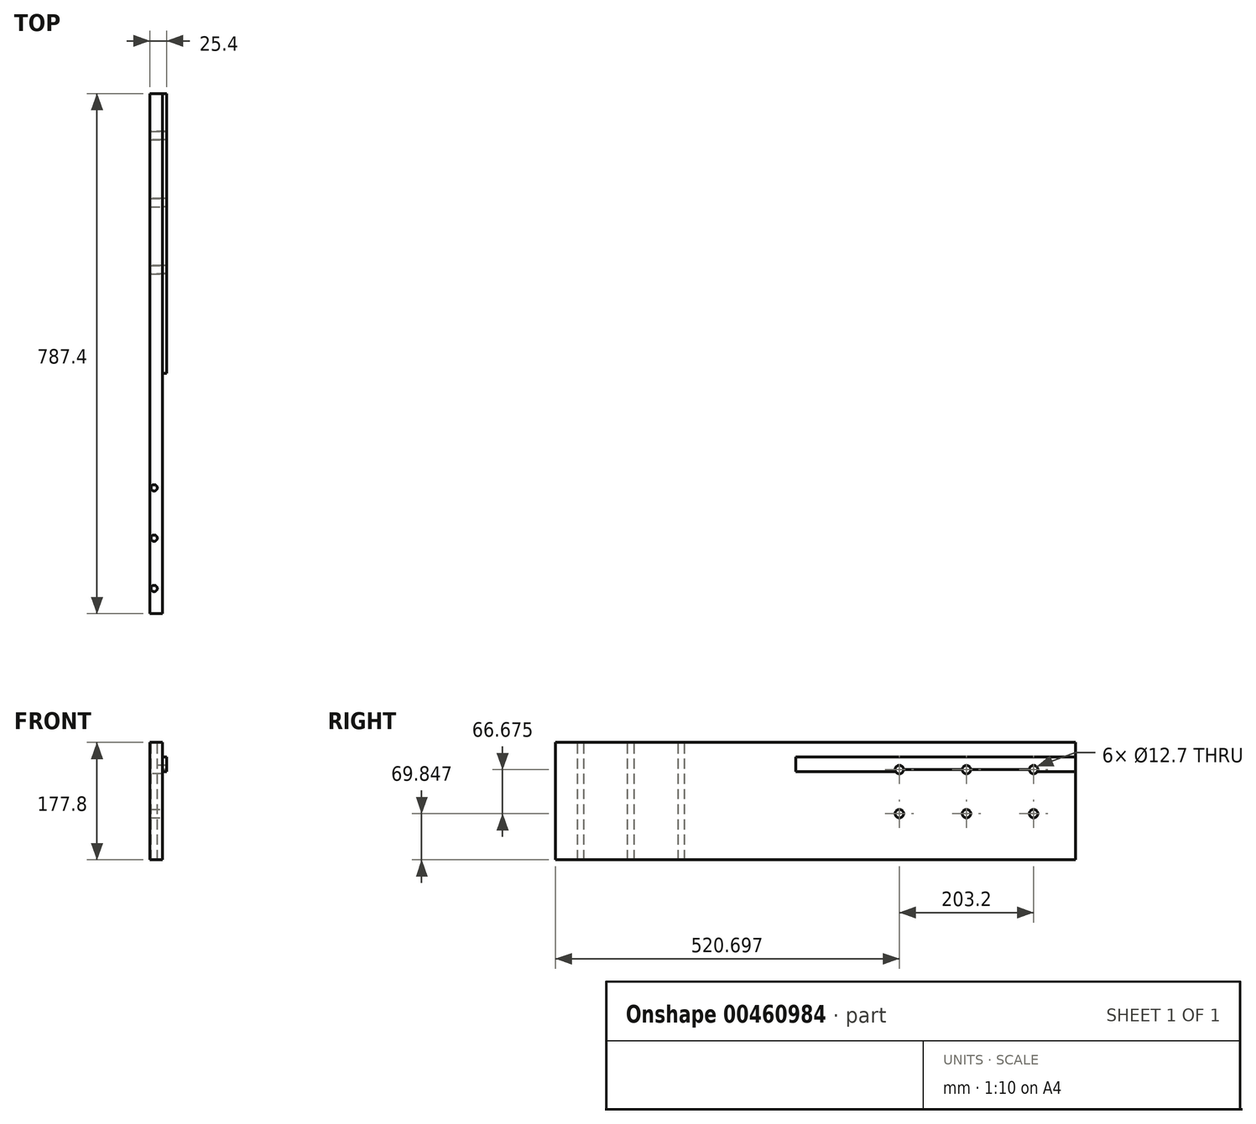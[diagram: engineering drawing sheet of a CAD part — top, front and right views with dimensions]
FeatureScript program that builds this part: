
annotation { "Feature Type Name" : "Feature", "Feature Type Description" : "" }
export const myFeature = defineFeature(function(context is Context, id is Id, definition is map)
    precondition{}
    {
        {
            var Q0;
            Q0=qCreatedBy(makeId("Right.planeOp"),FACE);
            var sketch = newSketch(context, id + "F0", { "sketchPlane" : qUnion([Q0])});
            skLineSegment(sketch, "E0.bottom", {"start": v(-363.93, 155.74) * mm, "end": v(423.47, 155.74) * mm});
            skLineSegment(sketch, "E0.top", {"start": v(-363.93, -22.06) * mm, "end": v(423.47, -22.06) * mm});
            skLineSegment(sketch, "E0.left", {"start": v(-363.93, 155.74) * mm, "end": v(-363.93, -22.06) * mm});
            skLineSegment(sketch, "E0.right", {"start": v(423.47, 155.74) * mm, "end": v(423.47, -22.06) * mm});
            skSolve(sketch);
        }
        {
            var Q0;
            Q0=makeQuery(id+"F0.imprint","IMPRINT",FACE,{"disambiguationData":[TD([[makeQuery(id+"F0.imprint","IMPRINT",EDGE,{"derivedFrom":sQuery(id+"F0.wireOp",EDGE,"E0.bottom")}),-1.0]])]});
            extrude(context, id + "F1", {"entities" : qUnion([Q0]), "depth" : 19.05 * mm});
        }
        {
            var Q0;
            Q0=makeQuery(id+"F1.opExtrude","CAP_FACE",FACE,{"disambiguationData":[OSD([sQuery(id+"F0.wireOp",EDGE,"E0.bottom"),sQuery(id+"F0.wireOp",EDGE,"E0.top"),sQuery(id+"F0.wireOp",EDGE,"E0.left"),sQuery(id+"F0.wireOp",EDGE,"E0.right")])],"isStart":false});
            var sketch = newSketch(context, id + "F2", { "sketchPlane" : qUnion([Q0])});
            skPoint(sketch, "E1", {"position": v(359.97, 47.79) * mm});
            skPoint(sketch, "E2", {"position": v(258.37, 47.79) * mm});
            skPoint(sketch, "E3", {"position": v(156.77, 47.79) * mm});
            skSolve(sketch);
        }
        {
            var Q0;
            Q0=makeQuery(id+"F1.opExtrude","SWEPT_FACE",FACE,{"disambiguationData":[OSD([sQuery(id+"F0.wireOp",EDGE,"E0.bottom")])]});
            var sketch = newSketch(context, id + "F3", { "sketchPlane" : qUnion([Q0])});
            skPoint(sketch, "E4", {"position": v(6.35, -325.83) * mm});
            skPoint(sketch, "E5", {"position": v(6.35, -249.63) * mm});
            skPoint(sketch, "E6", {"position": v(6.35, -173.43) * mm});
            skSolve(sketch);
        }
        {
            var Q0;
            Q0=sQuery(id+"F2.wireOp",VERTEX,"E3");
            var Q1;
            Q1=sQuery(id+"F2.wireOp",VERTEX,"E2");
            var Q2;
            Q2=sQuery(id+"F2.wireOp",VERTEX,"E1");
            var Q3;
            Q3=makeQuery(id+"F1.opExtrude","SWEPT_BODY",BODY,{"disambiguationData":[OSD([sQuery(id+"F0.wireOp",EDGE,"E0.bottom"),sQuery(id+"F0.wireOp",EDGE,"E0.top"),sQuery(id+"F0.wireOp",EDGE,"E0.left"),sQuery(id+"F0.wireOp",EDGE,"E0.right")])]});
            hole(context, id + "F4", {"style" : HoleStyle.SIMPLE, "endStyle" : HoleEndStyle.THROUGH, "holeDiameter" : 12.7 * mm, "isTappedThrough" : true, "tappedDepth" : 12.7 * mm, "tapClearance" : 3, "startFromSketch" : true, "locations" : qUnion([Q0, Q1, Q2]), "scope" : qUnion([Q3])});
        }
        {
            var Q0;
            Q0=sQuery(id+"F3.wireOp",VERTEX,"E6");
            var Q1;
            Q1=sQuery(id+"F3.wireOp",VERTEX,"E5");
            var Q2;
            Q2=sQuery(id+"F3.wireOp",VERTEX,"E4");
            var Q3;
            Q3=makeQuery(id+"F1.opExtrude","SWEPT_BODY",BODY,{"disambiguationData":[OSD([sQuery(id+"F0.wireOp",EDGE,"E0.bottom"),sQuery(id+"F0.wireOp",EDGE,"E0.top"),sQuery(id+"F0.wireOp",EDGE,"E0.left"),sQuery(id+"F0.wireOp",EDGE,"E0.right")])]});
            hole(context, id + "F5", {"style" : HoleStyle.SIMPLE, "endStyle" : HoleEndStyle.THROUGH, "holeDiameter" : 9.52 * mm, "isTappedThrough" : true, "tappedDepth" : 12.7 * mm, "tapClearance" : 3, "startFromSketch" : true, "locations" : qUnion([Q0, Q1, Q2]), "scope" : qUnion([Q3])});
        }
        {
            var Q0;
            Q0=makeQuery(id+"F1.opExtrude","CAP_FACE",FACE,{"disambiguationData":[OSD([sQuery(id+"F0.wireOp",EDGE,"E0.bottom"),sQuery(id+"F0.wireOp",EDGE,"E0.top"),sQuery(id+"F0.wireOp",EDGE,"E0.left"),sQuery(id+"F0.wireOp",EDGE,"E0.right")])],"isStart":false});
            var sketch = newSketch(context, id + "F6", { "sketchPlane" : qUnion([Q0])});
            skLineSegment(sketch, "E7", {"start": v(156.77, 47.79) * mm, "end": v(359.97, 47.79) * mm});
            skLineSegment(sketch, "E8.0", {"start": v(423.47, 133.51) * mm, "end": v(0, 133.51) * mm});
            skLineSegment(sketch, "E9.0", {"start": v(-370.28, 162.09) * mm, "end": v(-370.28, -28.41) * mm});
            skLineSegment(sketch, "E9.1", {"start": v(429.82, 162.09) * mm, "end": v(-370.28, 162.09) * mm});
            skLineSegment(sketch, "E9.2", {"start": v(429.82, -28.41) * mm, "end": v(429.82, 162.09) * mm});
            skLineSegment(sketch, "E9.3", {"start": v(-370.28, -28.41) * mm, "end": v(429.82, -28.41) * mm});
            skLineSegment(sketch, "E10", {"start": v(0, 133.51) * mm, "end": v(0, 111.29) * mm});
            skLineSegment(sketch, "E11", {"start": v(423.47, 111.29) * mm, "end": v(423.47, 133.51) * mm});
            skLineSegment(sketch, "E12.0", {"start": v(156.77, 114.46) * mm, "end": v(359.97, 114.46) * mm});
            skPoint(sketch, "E13", {"position": v(359.97, 114.46) * mm});
            skPoint(sketch, "E14", {"position": v(258.37, 114.46) * mm});
            skPoint(sketch, "E15", {"position": v(156.77, 114.46) * mm});
            skCircle(sketch, "E16", {"center": v(258.37, 114.46) * mm, "radius": 6.35 * mm});
            skCircle(sketch, "E17", {"center": v(359.97, 114.46) * mm, "radius": 6.35 * mm});
            skCircle(sketch, "E18", {"center": v(156.77, 114.46) * mm, "radius": 6.35 * mm});
            skLineSegment(sketch, "E19.0", {"start": v(423.47, 111.29) * mm, "end": v(0, 111.29) * mm});
            skPoint(sketch, "E20.orphan", {"position": v(0, 108.11) * mm});
            skSolve(sketch);
        }
        {
            var Q0;
            Q0=makeQuery(id+"F6.imprint","IMPRINT",FACE,{"disambiguationData":[TD([[makeQuery(id+"F6.imprint","IMPRINT",EDGE,{"derivedFrom":sQuery(id+"F6.wireOp",EDGE,"E8.0")}),1.0]])]});
            extrude(context, id + "F7", {"entities" : qUnion([Q0]), "operationType" : NewBodyOperationType.ADD, "depth" : 12.7 * mm, "hasOffset" : true, "offsetDistance" : 25.4 * mm, "symmetric" : true});
        }
        {
            var Q0;
            Q0=sQuery(id+"F6.wireOp",VERTEX,"E13");
            var Q1;
            Q1=sQuery(id+"F6.wireOp",VERTEX,"E14");
            var Q2;
            Q2=sQuery(id+"F6.wireOp",VERTEX,"E15");
            var Q3;
            Q3=makeQuery(id+"F1.opExtrude","SWEPT_BODY",BODY,{"disambiguationData":[OSD([sQuery(id+"F0.wireOp",EDGE,"E0.bottom"),sQuery(id+"F0.wireOp",EDGE,"E0.top"),sQuery(id+"F0.wireOp",EDGE,"E0.left"),sQuery(id+"F0.wireOp",EDGE,"E0.right")])]});
            hole(context, id + "F8", {"style" : HoleStyle.SIMPLE, "endStyle" : HoleEndStyle.THROUGH, "holeDiameter" : 12.7 * mm, "isTappedThrough" : true, "tappedDepth" : 12.7 * mm, "tapClearance" : 3, "startFromSketch" : true, "locations" : qUnion([Q0, Q1, Q2]), "scope" : qUnion([Q3])});
        }
    });
